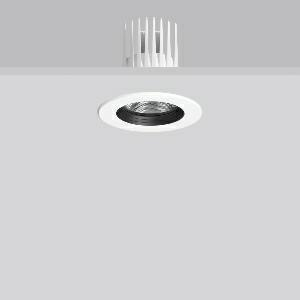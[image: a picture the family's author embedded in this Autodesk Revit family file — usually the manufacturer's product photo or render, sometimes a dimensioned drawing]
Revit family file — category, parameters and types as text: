
# Revit family: heledon_mini_e_901740_002_1_76_3875
name_source: partatom
category: Lighting Fixtures
units: mm (PartAtom-declared; Revit-internal decimal feet)

## family parameters
Cut with Voids When Loaded = No
Host = Face
Light Source = No
Part Type = Normal
Room Calculation Point = No
Round Connector Dimension = Use Diameter
Shared = No

## types (1)
- HELEDON mini E (1 x LED Modul 940, 2700 lm, 4000)
    Apparent Load = 20 VA
    Approval mark = CE
    CIE Flux Codes = 100 100 100 100 100
    Color Rendering = 92
    Color Temperature = 4000
    Default Elevation = 1800 mm
    Description = Series: HELEDON mini
Round recessed downlight. Housing: die-cast aluminium, powder-coated. Black plastic ring and recessed LED to prevent glare from the side. Optical assembly with reflector made of MIRO-Silver with 98% total light reflection for outstanding efficiency - can be changed without tools. Best colour rendering index Ra>90. Suitable for Recessed ceiling mounting. Installation without tools thanks to spring fastening system. Including separate LED converter with connecting cable 600 mm.High quality converter without flickering and stroboscopic effect. Through-wiring box (5 pole) available as accessory. The following accessories can be mounted without use of tools: interchangeable lenses, decorative glasses, honeycomb louvre, clear and frosted diffusers, white interchangeable plastic ring. 
Colour: traffic white, matt (RAL 9016)
Diameter: 124 mm
Height: 3 mm
Cut-out diameter: 114 mm
Recess height: 170 mm
Luminaire: recess height: 120 mm
Lamp: LED
Socket: without socket
Colour temperature: 4000K
Colour rendering index (CRI): 92
System power: 20 W
Rated luminous flux: 2700 lm
Luminous efficiency: 135 lm/W
Control gear: Converter, dimmable, DALI
Protection class: II
Type of protection: IP 20
    Height = 0 mm  [stored 0 ft]
    Lamp = 1 x LED Modul 940
    Lamp Light Flux = 2700 lm
    Lamp count = 1
    Length = 124 mm  [stored 0.406824 ft]
    Lifetime = 50000 h
    Luminous efficacy = 135 lm/W
    Manufacturer = RZB
    ModVariant = No
    Model = 901740.002.1.76
    Mounting Place = Ceiling
    Mounting Type = Recessed
    Number of Poles = 1
    OnlyDefault = Yes
    Power Factor = 1
    Product Name = HELEDON mini E
    Product group = Recessed downlights
    ProductGroupID = 402
    Protection Class = Protection class II
    Protection Degree = IP 20
    RLX_Detail_Level = 1
    RLX_Emergency_Light_Flux = 0 lm
    RLX_Emergency_Type = 0
    RLX_Emergency_Type_DB = No
    RlxData = <blob elided: 124973 chars, md5=ad32566b>
    Socket = socket
    Standby Power = 0 W
    System Light Flux = 2700 lm
    System Power = 20 W
    Type Comments = Product without accessories
    Type Image = 901657.002.jpg
    URL = http://relux.com
    VarID = ---
    Voltage = 230 V
    Voltage Range = 220-240 V
    Weight = 0.00 kg
    Width = 0 mm  [stored 0 ft]

note: [stored X ft] marks values corroborated as IEEE doubles in the binary element streams (Revit-internal decimal feet)

## geometry (parser evidence)
native form markers: Blend x4, Sweep x12
no freeform markers — native parametric forms only
